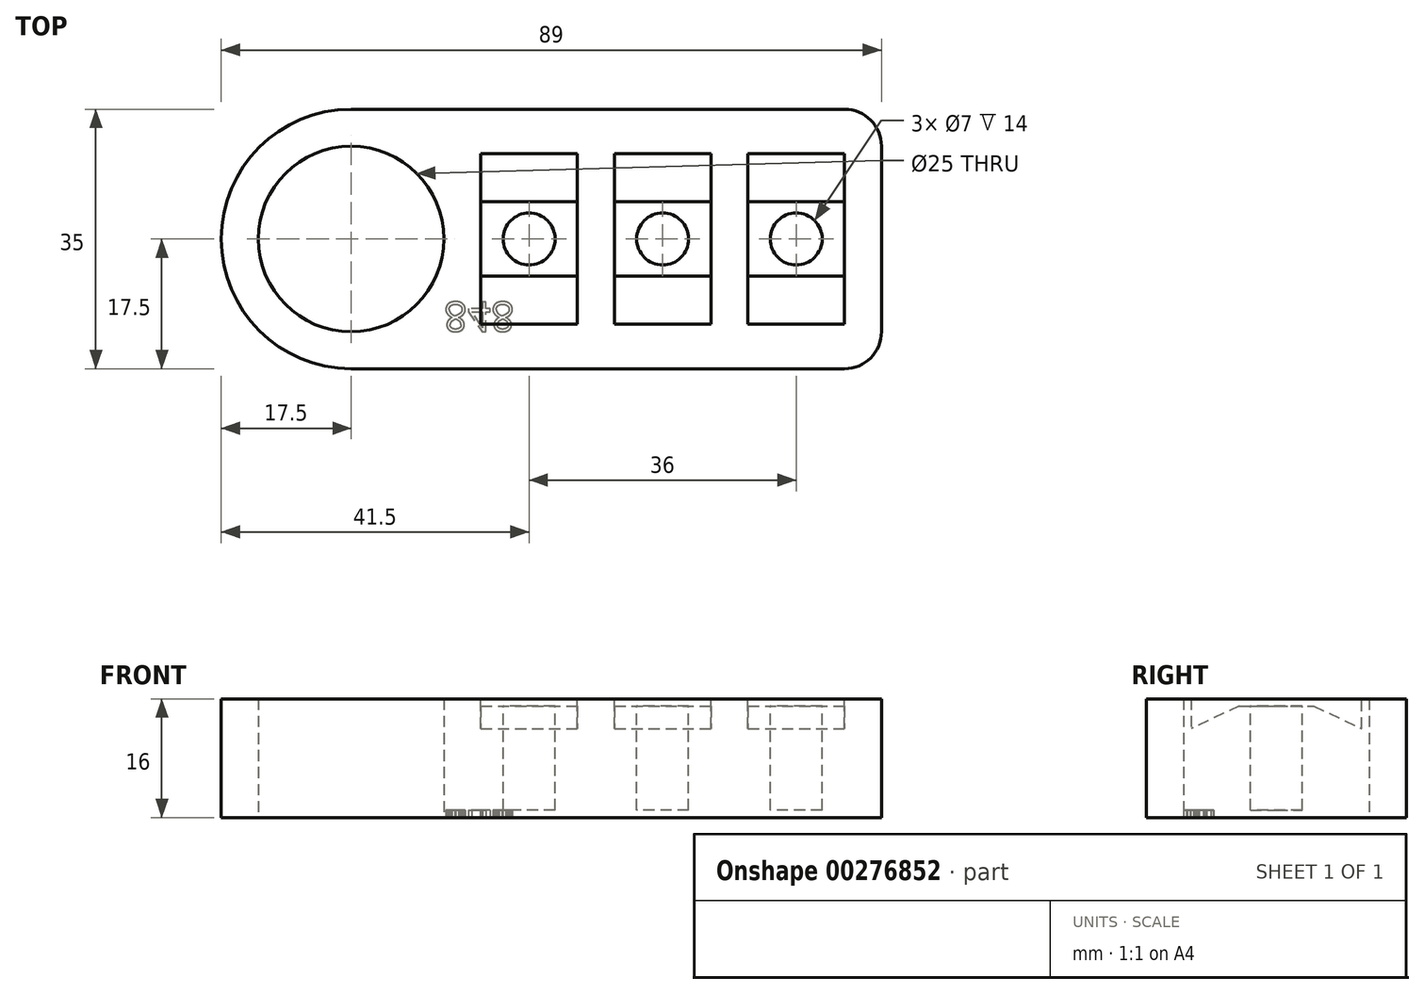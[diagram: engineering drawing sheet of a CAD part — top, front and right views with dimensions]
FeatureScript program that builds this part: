
annotation { "Feature Type Name" : "Feature", "Feature Type Description" : "" }
export const myFeature = defineFeature(function(context is Context, id is Id, definition is map)
    precondition{}
    {
        {
            var Q0;
            Q0=qCreatedBy(makeId("Top.planeOp"),FACE);
            var sketch = newSketch(context, id + "F0", { "sketchPlane" : qUnion([Q0])});
            skLineSegment(sketch, "E0.bottom", {"start": v(17.5, 0) * mm, "end": v(84, 0) * mm});
            skLineSegment(sketch, "E0.top", {"start": v(17.5, 35) * mm, "end": v(84, 35) * mm});
            skLineSegment(sketch, "E0.left", {"start": v(0, 17.5) * mm, "end": v(0, 17.5) * mm});
            skLineSegment(sketch, "E0.right", {"start": v(89, 5) * mm, "end": v(89, 30) * mm});
            skLineSegment(sketch, "E1.bottom", {"start": v(0, 0) * mm, "end": v(17.5, 0) * mm, "construction": true});
            skLineSegment(sketch, "E1.top", {"start": v(0, 17.5) * mm, "end": v(17.5, 17.5) * mm, "construction": true});
            skLineSegment(sketch, "E1.left", {"start": v(0, 0) * mm, "end": v(0, 17.5) * mm, "construction": true});
            skLineSegment(sketch, "E1.right", {"start": v(17.5, 0) * mm, "end": v(17.5, 17.5) * mm, "construction": true});
            skCircle(sketch, "E2", {"center": v(17.5, 17.5) * mm, "radius": 12.5 * mm});
            skPoint(sketch, "E3.visualSharp", {"position": v(0, 0) * mm});
            skArc(sketch, "E3.filletArc", {"start": v(0, 17.5) * mm, "mid": v(5.13, 5.13) * mm, "end": v(17.5, 0) * mm});
            skPoint(sketch, "E4.visualSharp", {"position": v(0, 35) * mm});
            skArc(sketch, "E4.filletArc", {"start": v(17.5, 35) * mm, "mid": v(5.13, 29.87) * mm, "end": v(0, 17.5) * mm});
            skPoint(sketch, "E5.visualSharp", {"position": v(89, 35) * mm});
            skArc(sketch, "E5.filletArc", {"start": v(89, 30) * mm, "mid": v(87.54, 33.54) * mm, "end": v(84, 35) * mm});
            skPoint(sketch, "E6.visualSharp", {"position": v(89, 0) * mm});
            skArc(sketch, "E6.filletArc", {"start": v(84, 0) * mm, "mid": v(87.54, 1.46) * mm, "end": v(89, 5) * mm});
            skSolve(sketch);
        }
        {
            var Q0;
            Q0=makeQuery(id+"F0.imprint","IMPRINT",FACE,{"disambiguationData":[TD([[makeQuery(id+"F0.imprint","IMPRINT",EDGE,{"derivedFrom":sQuery(id+"F0.wireOp",EDGE,"E0.bottom")}),1.0]])]});
            extrude(context, id + "F1", {"entities" : qUnion([Q0]), "depth" : 16 * mm});
        }
        {
            var Q0;
            Q0=makeQuery(id+"F1.opExtrude","SWEPT_FACE",FACE,{"disambiguationData":[OSD([sQuery(id+"F0.wireOp",EDGE,"E0.right")])]});
            var sketch = newSketch(context, id + "F2", { "sketchPlane" : qUnion([Q0])});
            skLineSegment(sketch, "E7.bottom", {"start": v(0, 0) * mm, "end": v(6, 0) * mm, "construction": true});
            skLineSegment(sketch, "E7.top", {"start": v(0, 12) * mm, "end": v(6, 12) * mm, "construction": true});
            skLineSegment(sketch, "E7.left", {"start": v(0, 0) * mm, "end": v(0, 12) * mm, "construction": true});
            skLineSegment(sketch, "E7.right", {"start": v(6, 0) * mm, "end": v(6, 12) * mm, "construction": true});
            skLineSegment(sketch, "E8", {"start": v(6, 12) * mm, "end": v(29, 12) * mm, "construction": true});
            skLineSegment(sketch, "E9.bottom", {"start": v(6, 12) * mm, "end": v(12.5, 12) * mm, "construction": true});
            skLineSegment(sketch, "E9.top", {"start": v(6, 15) * mm, "end": v(12.5, 15) * mm, "construction": true});
            skLineSegment(sketch, "E9.left", {"start": v(6, 12) * mm, "end": v(6, 15) * mm, "construction": true});
            skLineSegment(sketch, "E9.right", {"start": v(12.5, 12) * mm, "end": v(12.5, 15) * mm, "construction": true});
            skLineSegment(sketch, "E10", {"start": v(12.5, 15) * mm, "end": v(6, 12) * mm});
            skLineSegment(sketch, "E11", {"start": v(12.5, 15) * mm, "end": v(22.5, 15) * mm});
            skLineSegment(sketch, "E12", {"start": v(22.5, 15) * mm, "end": v(29, 12) * mm});
            skLineSegment(sketch, "E13", {"start": v(29, 12) * mm, "end": v(29, 16) * mm});
            skLineSegment(sketch, "E14", {"start": v(29, 16) * mm, "end": v(6, 16) * mm});
            skLineSegment(sketch, "E15", {"start": v(6, 16) * mm, "end": v(6, 12) * mm});
            skSolve(sketch);
        }
        {
            var Q0;
            Q0=makeQuery(id+"F2.imprint","IMPRINT",FACE,{"disambiguationData":[TD([[makeQuery(id+"F2.imprint","IMPRINT",EDGE,{"derivedFrom":sQuery(id+"F2.wireOp",EDGE,"E10")}),-1.0]])]});
            extrude(context, id + "F3", {"entities" : qUnion([Q0]), "operationType" : NewBodyOperationType.REMOVE, "oppositeDirection" : true, "depth" : 18 * mm, "hasSecondDirection" : true, "secondDirectionOppositeDirection" : true, "secondDirectionDepth" : 5 * mm});
        }
        {
            var Q0;
            Q0=makeQuery(id+"F2.imprint","IMPRINT",FACE,{"disambiguationData":[TD([[makeQuery(id+"F2.imprint","IMPRINT",EDGE,{"derivedFrom":sQuery(id+"F2.wireOp",EDGE,"E10")}),-1.0]])]});
            extrude(context, id + "F4", {"entities" : qUnion([Q0]), "operationType" : NewBodyOperationType.REMOVE, "oppositeDirection" : true, "depth" : 36 * mm, "hasSecondDirection" : true, "secondDirectionOppositeDirection" : true, "secondDirectionDepth" : 23 * mm});
        }
        {
            var Q0;
            Q0=makeQuery(id+"F2.imprint","IMPRINT",FACE,{"disambiguationData":[TD([[makeQuery(id+"F2.imprint","IMPRINT",EDGE,{"derivedFrom":sQuery(id+"F2.wireOp",EDGE,"E10")}),-1.0]])]});
            extrude(context, id + "F5", {"entities" : qUnion([Q0]), "operationType" : NewBodyOperationType.REMOVE, "oppositeDirection" : true, "depth" : 54 * mm, "hasSecondDirection" : true, "secondDirectionOppositeDirection" : true, "secondDirectionDepth" : 41 * mm});
        }
        {
            var Q0;
            Q0=makeQuery(id+"F5.boolean.opBoolean","COPY",FACE,{"derivedFrom":makeQuery(id+"F5.opExtrude","SWEPT_FACE",FACE,{"disambiguationData":[OSD([sQuery(id+"F2.wireOp",EDGE,"E11")])]})});
            var sketch = newSketch(context, id + "F6", { "sketchPlane" : qUnion([Q0])});
            skLineSegment(sketch, "E16.0.0", {"start": v(66, 12.5) * mm, "end": v(66, 22.5) * mm, "construction": true});
            skLineSegment(sketch, "E16.0.1", {"start": v(66, 22.5) * mm, "end": v(53, 22.5) * mm, "construction": true});
            skLineSegment(sketch, "E16.0.2", {"start": v(53, 22.5) * mm, "end": v(53, 12.5) * mm, "construction": true});
            skLineSegment(sketch, "E16.0.3", {"start": v(53, 12.5) * mm, "end": v(66, 12.5) * mm, "construction": true});
            skLineSegment(sketch, "E17.0.0", {"start": v(84, 12.5) * mm, "end": v(84, 22.5) * mm, "construction": true});
            skLineSegment(sketch, "E17.0.1", {"start": v(84, 22.5) * mm, "end": v(71, 22.5) * mm, "construction": true});
            skLineSegment(sketch, "E17.0.2", {"start": v(71, 22.5) * mm, "end": v(71, 12.5) * mm, "construction": true});
            skLineSegment(sketch, "E17.0.3", {"start": v(71, 12.5) * mm, "end": v(84, 12.5) * mm, "construction": true});
            skLineSegment(sketch, "E18.0.0", {"start": v(48, 12.5) * mm, "end": v(48, 22.5) * mm, "construction": true});
            skLineSegment(sketch, "E18.0.1", {"start": v(48, 22.5) * mm, "end": v(35, 22.5) * mm, "construction": true});
            skLineSegment(sketch, "E18.0.2", {"start": v(35, 22.5) * mm, "end": v(35, 12.5) * mm, "construction": true});
            skLineSegment(sketch, "E18.0.3", {"start": v(35, 12.5) * mm, "end": v(48, 12.5) * mm, "construction": true});
            skLineSegment(sketch, "E19", {"start": v(35, 12.5) * mm, "end": v(48, 22.5) * mm, "construction": true});
            skLineSegment(sketch, "E20", {"start": v(53, 12.5) * mm, "end": v(66, 22.5) * mm, "construction": true});
            skLineSegment(sketch, "E21", {"start": v(71, 12.5) * mm, "end": v(84, 22.5) * mm, "construction": true});
            skCircle(sketch, "E22", {"center": v(41.5, 17.5) * mm, "radius": 3.5 * mm});
            skCircle(sketch, "E23", {"center": v(59.5, 17.5) * mm, "radius": 3.5 * mm});
            skCircle(sketch, "E24", {"center": v(77.5, 17.5) * mm, "radius": 3.5 * mm});
            skSolve(sketch);
        }
        {
            var Q0;
            Q0=makeQuery(id+"F6.imprint","IMPRINT",FACE,{"disambiguationData":[TD([[makeQuery(id+"F6.imprint","IMPRINT",EDGE,{"derivedFrom":sQuery(id+"F6.wireOp",EDGE,"E22")}),1.0]])]});
            var Q1;
            Q1=makeQuery(id+"F6.imprint","IMPRINT",FACE,{"disambiguationData":[TD([[makeQuery(id+"F6.imprint","IMPRINT",EDGE,{"derivedFrom":sQuery(id+"F6.wireOp",EDGE,"E23")}),1.0]])]});
            var Q2;
            Q2=makeQuery(id+"F6.imprint","IMPRINT",FACE,{"disambiguationData":[TD([[makeQuery(id+"F6.imprint","IMPRINT",EDGE,{"derivedFrom":sQuery(id+"F6.wireOp",EDGE,"E24")}),1.0]])]});
            extrude(context, id + "F7", {"entities" : qUnion([Q0, Q1, Q2]), "operationType" : NewBodyOperationType.REMOVE, "oppositeDirection" : true, "depth" : 14 * mm});
        }
        {
            var Q0;
            Q0=makeQuery(id+"F1.opExtrude","CAP_FACE",FACE,{"disambiguationData":[OSD([sQuery(id+"F0.wireOp",EDGE,"E0.bottom"),sQuery(id+"F0.wireOp",EDGE,"E0.top"),sQuery(id+"F0.wireOp",EDGE,"E0.right"),sQuery(id+"F0.wireOp",EDGE,"E2"),sQuery(id+"F0.wireOp",EDGE,"E3.filletArc"),sQuery(id+"F0.wireOp",EDGE,"E4.filletArc"),sQuery(id+"F0.wireOp",EDGE,"E5.filletArc"),sQuery(id+"F0.wireOp",EDGE,"E6.filletArc")])],"isStart":true});
            var sketch = newSketch(context, id + "F8", { "sketchPlane" : qUnion([Q0])});
            skLineSegment(sketch, "E25.bottom", {"start": v(0, 0) * mm, "end": v(30, 0) * mm, "construction": true});
            skLineSegment(sketch, "E25.top", {"start": v(0, -5) * mm, "end": v(30, -5) * mm, "construction": true});
            skLineSegment(sketch, "E25.left", {"start": v(0, 0) * mm, "end": v(0, -5) * mm, "construction": true});
            skLineSegment(sketch, "E25.right", {"start": v(30, 0) * mm, "end": v(30, -5) * mm, "construction": true});
            skText(sketch, "E26", { "text": "848", "fontName": "OpenSans-Regular.ttf"});
            const initialGuessF8  = {"E26": [0.03, -0.009, 1, 0, 0.004]};
            skSetInitialGuess(sketch, initialGuessF8);
            skSolve(sketch);
        }
        {
            var Q0;
            Q0 = qSketchRegion(id + "F8", true);
            extrude(context, id + "F9", {"entities" : qUnion([Q0]), "operationType" : NewBodyOperationType.REMOVE, "oppositeDirection" : true, "depth" : 1 * mm});
        }
    });
